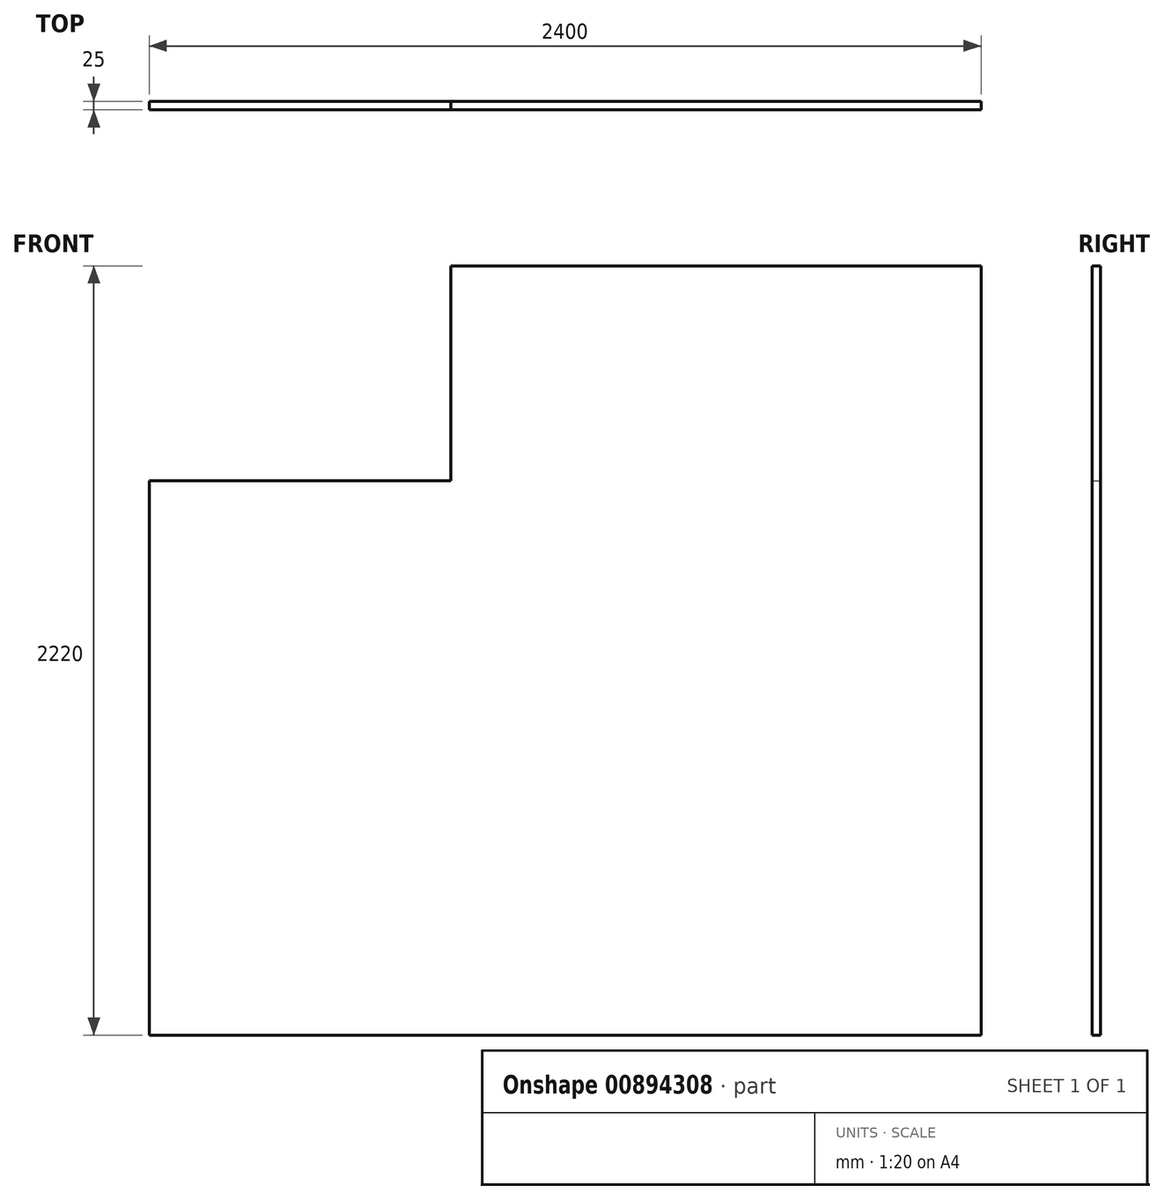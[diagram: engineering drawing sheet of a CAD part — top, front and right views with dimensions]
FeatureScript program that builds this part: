
annotation { "Feature Type Name" : "Feature", "Feature Type Description" : "" }
export const myFeature = defineFeature(function(context is Context, id is Id, definition is map)
    precondition{}
    {
        {
            var Q0;
            Q0=qCreatedBy(makeId("Front.planeOp"),FACE);
            var sketch = newSketch(context, id + "F0", { "sketchPlane" : qUnion([Q0])});
            skLineSegment(sketch, "E0", {"start": v(-330, 1110) * mm, "end": v(1200, 1110) * mm});
            skLineSegment(sketch, "E1", {"start": v(-330, 1110) * mm, "end": v(-330, 490) * mm});
            skLineSegment(sketch, "E2", {"start": v(-330, 490) * mm, "end": v(-1200, 490) * mm});
            skLineSegment(sketch, "E3", {"start": v(1200, 1110) * mm, "end": v(1200, -1110) * mm});
            skLineSegment(sketch, "E4", {"start": v(-977.65, -1110) * mm, "end": v(1200, -1110) * mm});
            skLineSegment(sketch, "E5", {"start": v(-1200, 490) * mm, "end": v(-1200, -1110) * mm});
            skLineSegment(sketch, "E6", {"start": v(-1200, -1110) * mm, "end": v(-977.65, -1110) * mm});
            skSolve(sketch);
        }
        {
            var Q0;
            Q0=makeQuery(id+"F0.imprint","IMPRINT",FACE,{"disambiguationData":[TD([[makeQuery(id+"F0.imprint","IMPRINT",EDGE,{"derivedFrom":sQuery(id+"F0.wireOp",EDGE,"E0")}),-1.0]])]});
            extrude(context, id + "F1", {"entities" : qUnion([Q0]), "depth" : 25 * mm, "offsetDistance" : 25 * mm});
        }
    });
